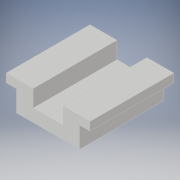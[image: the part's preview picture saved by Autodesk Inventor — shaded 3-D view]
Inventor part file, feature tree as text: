
AUTODESK INVENTOR PART (.ipt)
format: ipt  version: 2019 (Build 230136000, 136)  size: 119,296 bytes
history: native  units: in
note: dims shown in document units (in); Inventor stores cm internally (conversion verified against a paired STEP export)
features: extrude x3, sketch x3, projected_geometry x1
ambient origin geometry x8: Origin, YZ Plane, XZ Plane, XY Plane, X Axis, Y Axis, Z Axis, Center Point
bodies: Solid1 (feature_tree)
feature tree (7):
  extrude  "Extrusion1"  Depth=0.7874in
  extrude  "Extrusion2"  Depth=0.2807in
  extrude  "Extrusion3"  Depth=0.0984in
  sketch  "Sketch1"  dims[d0=0.7874in d1=0.7874in]
  sketch  "Sketch2"  dims[d2=0.1181in d3=0.0in d5=0.2807in]
  projected_geometry  "Projected Loop1"
  sketch  "Sketch3"  dims[d6=0.1575in d7=0.0in d8=0.0984in d9=0.1969in d10=0.0787in d11=0.0in]
